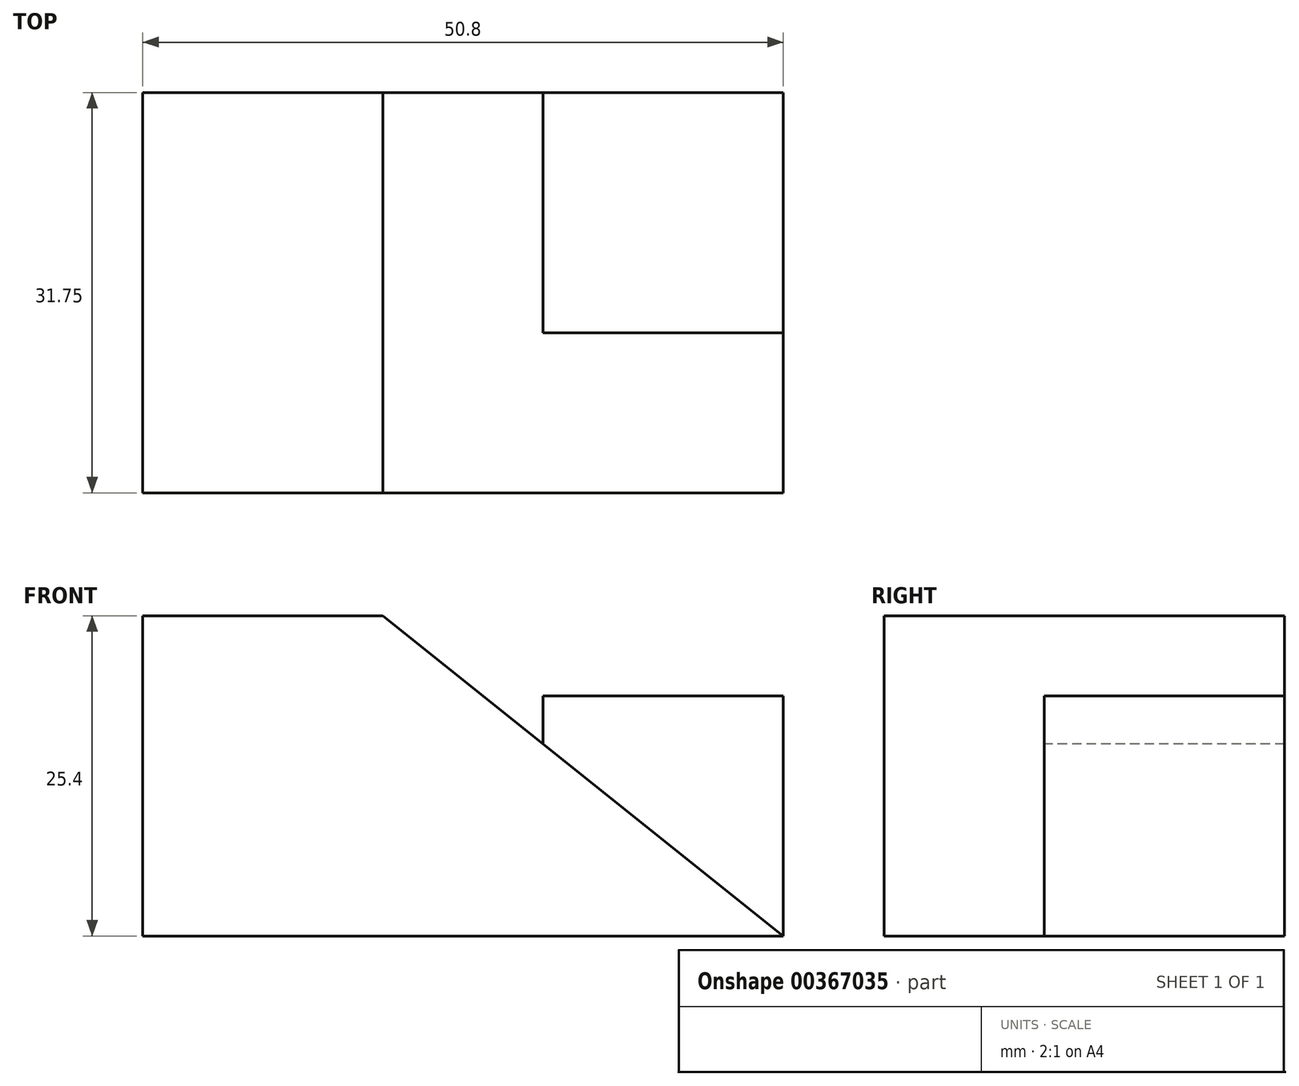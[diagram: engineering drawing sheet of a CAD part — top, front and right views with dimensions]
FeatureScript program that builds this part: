
annotation { "Feature Type Name" : "Feature", "Feature Type Description" : "" }
export const myFeature = defineFeature(function(context is Context, id is Id, definition is map)
    precondition{}
    {
        {
            var Q0;
            Q0=qCreatedBy(makeId("Top.planeOp"),FACE);
            var sketch = newSketch(context, id + "F0", { "sketchPlane" : qUnion([Q0])});
            skLineSegment(sketch, "E0", {"start": v(0, 0) * mm, "end": v(50.8, 0) * mm});
            skLineSegment(sketch, "E1", {"start": v(50.8, 0) * mm, "end": v(50.8, 31.75) * mm});
            skLineSegment(sketch, "E2", {"start": v(50.8, 31.75) * mm, "end": v(0, 31.75) * mm});
            skLineSegment(sketch, "E3", {"start": v(0, 31.75) * mm, "end": v(0, 0) * mm});
            skSolve(sketch);
        }
        {
            var Q0;
            Q0 = qSketchRegion(id + "F0", true);
            extrude(context, id + "F1", {"entities" : qUnion([Q0]), "depth" : 25.4 * mm});
        }
        {
            var Q0;
            Q0=makeQuery(id+"F1.opExtrude","SWEPT_FACE",FACE,{"disambiguationData":[OSD([sQuery(id+"F0.wireOp",EDGE,"E0")])]});
            var sketch = newSketch(context, id + "F2", { "sketchPlane" : qUnion([Q0])});
            skLineSegment(sketch, "E4", {"start": v(50.8, 0) * mm, "end": v(19.05, 25.4) * mm});
            skSolve(sketch);
        }
        {
            var Q0;
            {var subQ0=sQuery(id+"F2.wireOp",EDGE,"E4");Q0=makeQuery(id+"F2.imprint","IMPRINT",FACE,{"disambiguationData":[TD([[makeQuery(id+"F2.imprint","IMPRINT",EDGE,{"derivedFrom":subQ0}),-1.0]])]});}
            extrude(context, id + "F3", {"entities" : qUnion([Q0]), "operationType" : NewBodyOperationType.REMOVE, "oppositeDirection" : true, "depth" : 31.75 * mm});
        }
        {
            var Q0;
            Q0=makeQuery(id+"F1.opExtrude","CAP_FACE",FACE,{"disambiguationData":[OSD([sQuery(id+"F0.wireOp",EDGE,"E0"),sQuery(id+"F0.wireOp",EDGE,"E1"),sQuery(id+"F0.wireOp",EDGE,"E2"),sQuery(id+"F0.wireOp",EDGE,"E3")])],"isStart":true});
            var sketch = newSketch(context, id + "F4", { "sketchPlane" : qUnion([Q0])});
            skLineSegment(sketch, "E5", {"start": v(50.8, -12.7) * mm, "end": v(31.75, -12.7) * mm});
            skLineSegment(sketch, "E6", {"start": v(31.75, -12.7) * mm, "end": v(31.75, -31.75) * mm});
            skSolve(sketch);
        }
        {
            var Q0;
            {var subQ0=sQuery(id+"F4.wireOp",EDGE,"E5");Q0=makeQuery(id+"F4.imprint","IMPRINT",FACE,{"disambiguationData":[TD([[makeQuery(id+"F4.imprint","IMPRINT",EDGE,{"derivedFrom":subQ0}),1.0]])]});}
            extrude(context, id + "F5", {"entities" : qUnion([Q0]), "operationType" : NewBodyOperationType.ADD, "oppositeDirection" : true, "depth" : 19.05 * mm});
        }
    });
